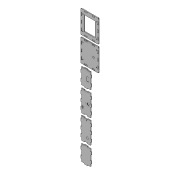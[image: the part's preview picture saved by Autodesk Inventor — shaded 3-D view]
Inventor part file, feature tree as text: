
AUTODESK INVENTOR PART (.ipt)
format: ipt  version: 2021.3 (Build 253353000, 353)  size: 1,478,144 bytes
history: native  units: in
note: dims shown in document units (in); Inventor stores cm internally (conversion verified against a paired STEP export)
features: other x8, extrude x8, sketch x5, projected_geometry x4, fillet x1
ambient origin geometry x8: Origin, YZ Plane, XZ Plane, XY Plane, X Axis, Y Axis, Z Axis, Center Point
bodies: Volumenkörper1 (feature_tree), Volumenkörper2 (feature_tree), Volumenkörper3 (feature_tree), Volumenkörper4 (feature_tree), Volumenkörper5 (feature_tree), Volumenkörper6 (feature_tree)
feature tree (26):
  other  "Bauteil1.ipt"
  sketch  "Skizze1"  dims[d0=0.3937in d4=0.1575in]
  extrude  "Extrusion1"  Depth=0.1575in
  extrude  "Extrusion2"  Depth=0.747in
  sketch  "Skizze2"  dims[d5=0.6932in d6=0.747in]
  extrude  "Extrusion3"  Depth=0.3937in TaperAngle=0.0deg
  extrude  "Extrusion4"  Depth=0.1969in
  fillet  "Rundung1"  Radius=0.7874in
  extrude  "Extrusion5"  Depth=0.3937in TaperAngle=0.0deg
  extrude  "Extrusion6"  Depth=0.3937in TaperAngle=0.0deg
  sketch  "Skizze5"  dims[d14=0.3937in d15=0.3937in d16=0.0in d17=0.3937in d18=0.0in d19=0.0787in d20=0.0591in d21=0.8858in d22=0.4724in d23=0.2362in d24=1.1811in d26=360.0deg d28=0.3937in d29=0.0in d30=0.3937in d31=0.0in d32=0.315in d33=0.1575in d34=0.2756in d35=0.1378in d36=0.3937in d37=0.0in d38=0.3937in d39=0.0in]
  extrude  "Extrusion7"  Depth=0.0787in
  extrude  "Extrusion8"  Depth=0.3937in
  other  "Volumenkörper1::Bauteil1.ipt"
  other  "Volumenkörper2::Bauteil1.ipt"
  other  "Volumenkörper3::Bauteil1.ipt"
  other  "Volumenkörper4::Bauteil1.ipt"
  other  "Volumenkörper5::Bauteil1.ipt"
  other  "Volumenkörper6::Bauteil1.ipt"
  other  "Bezeichnung1"
  projected_geometry  "Projizierte Kontur1"
  projected_geometry  "Projizierte Kontur2"
  sketch  "Skizze3"  dims[d7=0.3937in d8=0.0in d9=0.3937in d10=0.0in]
  sketch  "Skizze4"  dims[d11=0.1181in d12=0.1969in d13=0.7874in]
  projected_geometry  "Projizierte Kontur3"
  projected_geometry  "Projizierte Kontur4"
